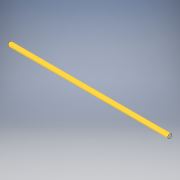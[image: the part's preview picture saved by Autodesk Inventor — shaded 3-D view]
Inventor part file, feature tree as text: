
AUTODESK INVENTOR PART (.ipt)
format: ipt  version: 2019 (Build 230136000, 136)  size: 95,744 bytes
history: native  units: in
note: dims shown in document units (in); Inventor stores cm internally (conversion verified against a paired STEP export)
features: extrude x1, sketch x1
ambient origin geometry x8: Origin, YZ Plane, XZ Plane, XY Plane, X Axis, Y Axis, Z Axis, Center Point
bodies: Solid1 (feature_tree)
feature tree (2):
  extrude  "Extrusion1"  Depth=11.811in TaperAngle=0.0deg
  sketch  "Sketch1"  dims[d0=0.315in d1=11.811in d2=0.0in]
